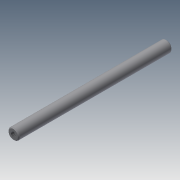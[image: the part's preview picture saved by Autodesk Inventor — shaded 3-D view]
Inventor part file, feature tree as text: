
AUTODESK INVENTOR PART (.ipt)
format: ipt  version: 2013 (Build 170138000, 138)  size: 79,872 bytes
history: native  units: mm
features: sketch x3, hole x2, extrude x1, chamfer x1
ambient origin geometry x8: Origin, YZ Plane, XZ Plane, XY Plane, X Axis, Y Axis, Z Axis, Center Point
bodies: Solid1 (feature_tree)
feature tree (7):
  extrude  "Extrusion1"  Depth=82.6mm TaperAngle=0.0deg
  hole  "Hole1"  [1 undecoded]
  hole  "Hole2"  [1 undecoded]
  chamfer  "Chamfer1"  [1 undecoded]
  sketch  "Sketch1"  dims[d0=6.0mm d1=82.6mm d2=0.0mm]
  sketch  "Sketch2"  dims[d3=2.459mm d4=6.0mm d5=4.0mm d6=2.0mm d7=90.0deg d8=8.0mm d9=0.0mm]
  sketch  "Sketch3"  dims[d10=2.459mm d11=6.0mm d12=4.0mm d13=2.0mm d14=90.0deg d15=8.0mm d16=0.0mm d17=0.5mm d18=2.0mm d19=45.0deg]
note: 3 required parameter values undecoded (feature->parameter linkage not recoverable at this tier; creation-order binding heuristic only, values carry confidence <= 0.55)
